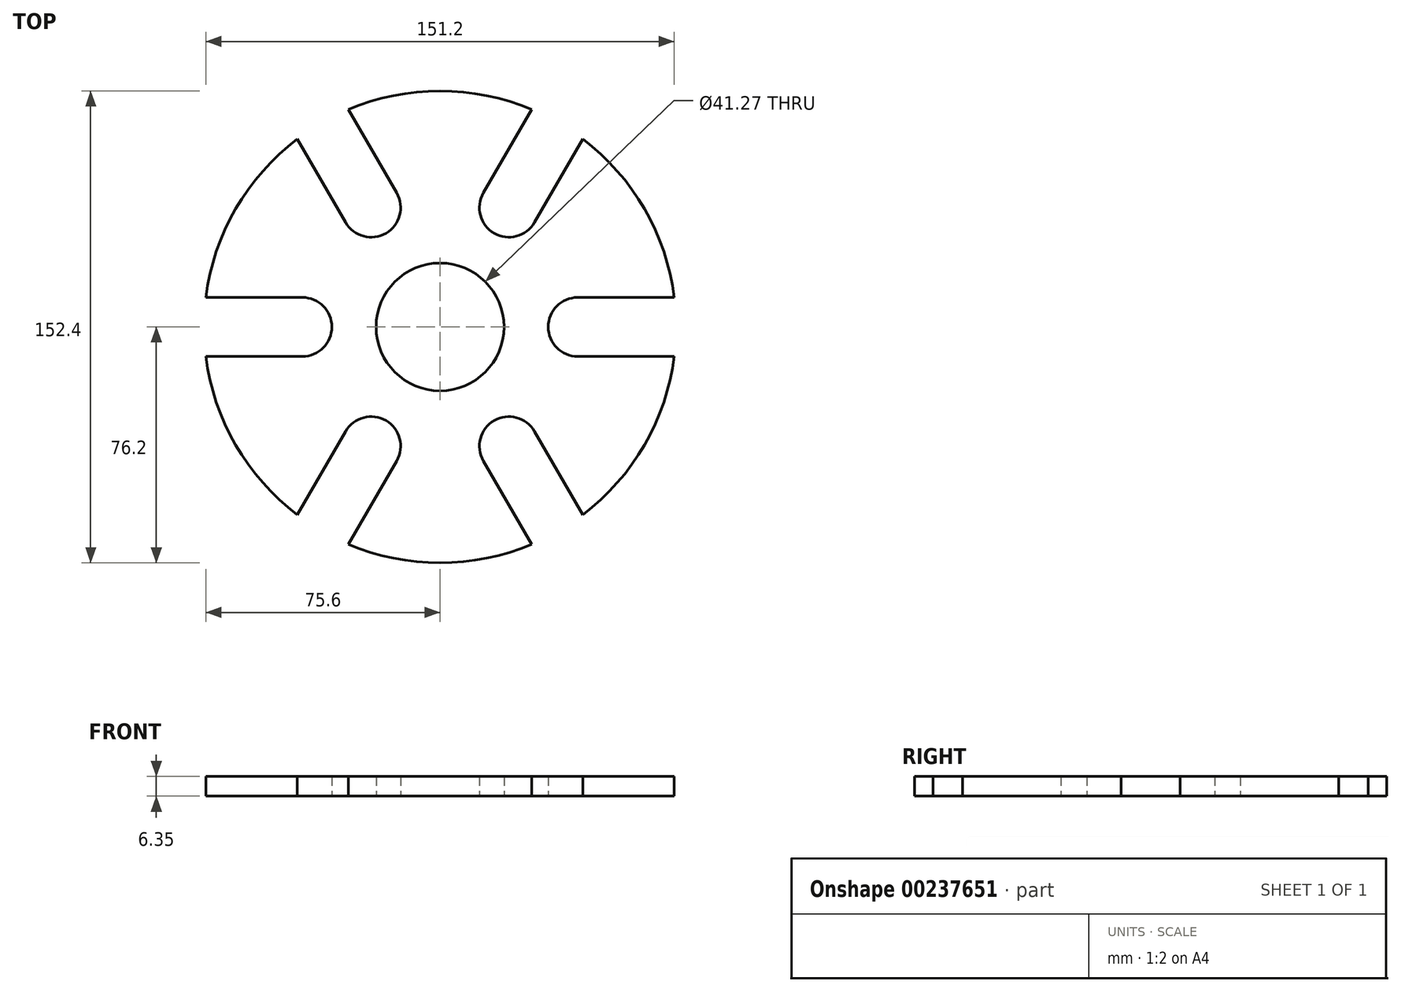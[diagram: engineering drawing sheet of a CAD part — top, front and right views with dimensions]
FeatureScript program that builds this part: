
annotation { "Feature Type Name" : "Feature", "Feature Type Description" : "" }
export const myFeature = defineFeature(function(context is Context, id is Id, definition is map)
    precondition{}
    {
        {
            var Q0;
            Q0=qCreatedBy(makeId("Top.planeOp"),FACE);
            var sketch = newSketch(context, id + "F0", { "sketchPlane" : qUnion([Q0])});
            skArc(sketch, "E0", {"start": v(-75.6, -9.52) * mm, "mid": v(-66, -38.1) * mm, "end": v(-46.05, -60.71) * mm});
            skCircle(sketch, "E1", {"center": v(0, 0) * mm, "radius": 20.64 * mm});
            skArc(sketch, "E2", {"start": v(-44.45, -9.53) * mm, "mid": v(-34.93, 0) * mm, "end": v(-44.45, 9.53) * mm});
            skLineSegment(sketch, "E3", {"start": v(-44.45, 9.53) * mm, "end": v(-75.6, 9.53) * mm});
            skLineSegment(sketch, "E4", {"start": v(-44.45, -9.53) * mm, "end": v(-75.6, -9.53) * mm});
            skLineSegment(sketch, "E5", {"start": v(-75.6, -9.53) * mm, "end": v(-44.45, -9.53) * mm});
            skLineSegment(sketch, "E6.MirrorCS", {"start": v(44.45, -9.53) * mm, "end": v(75.6, -9.53) * mm});
            skArc(sketch, "E7.MirrorC", {"start": v(-75.6, 9.53) * mm, "mid": v(-66, 38.1) * mm, "end": v(-46.05, 60.71) * mm});
            skArc(sketch, "E8.MirrorC", {"start": v(44.45, -9.53) * mm, "mid": v(34.93, 0) * mm, "end": v(44.45, 9.53) * mm});
            skLineSegment(sketch, "E9.MirrorCS", {"start": v(75.6, -9.53) * mm, "end": v(44.45, -9.53) * mm});
            skLineSegment(sketch, "E10.MirrorCS", {"start": v(44.45, 9.53) * mm, "end": v(75.6, 9.53) * mm});
            skArc(sketch, "E11.trimOffspring", {"start": v(75.6, -9.52) * mm, "mid": v(66, -38.1) * mm, "end": v(46.05, -60.71) * mm});
            skArc(sketch, "E12.trimOffspring", {"start": v(75.6, 9.53) * mm, "mid": v(66, 38.1) * mm, "end": v(46.05, 60.71) * mm});
            skArc(sketch, "E13", {"start": v(13.98, 43.26) * mm, "mid": v(17.46, 30.25) * mm, "end": v(30.47, 33.73) * mm});
            skLineSegment(sketch, "E14", {"start": v(30.47, 33.73) * mm, "end": v(46.05, 60.71) * mm});
            skLineSegment(sketch, "E15", {"start": v(46.05, 60.71) * mm, "end": v(30.47, 33.73) * mm});
            skLineSegment(sketch, "E16", {"start": v(13.98, 43.26) * mm, "end": v(29.55, 70.24) * mm});
            skArc(sketch, "E17.trimOffspring", {"start": v(29.55, 70.24) * mm, "mid": v(0, 76.2) * mm, "end": v(-29.55, 70.24) * mm});
            skArc(sketch, "E18.trimOffspring", {"start": v(46.05, 60.71) * mm, "mid": v(66, 38.1) * mm, "end": v(75.6, 9.53) * mm});
            skLineSegment(sketch, "E19.MirrorCS", {"start": v(-13.98, -43.26) * mm, "end": v(-29.55, -70.24) * mm});
            skLineSegment(sketch, "E20.MirrorCS", {"start": v(-30.47, -33.73) * mm, "end": v(-46.05, -60.71) * mm});
            skLineSegment(sketch, "E21.MirrorCS", {"start": v(-29.55, -70.24) * mm, "end": v(-13.98, -43.26) * mm});
            skArc(sketch, "E22.MirrorCS", {"start": v(-30.47, -33.73) * mm, "mid": v(-17.46, -30.25) * mm, "end": v(-13.98, -43.26) * mm});
            skArc(sketch, "E23.trimOffspring", {"start": v(-29.55, -70.24) * mm, "mid": v(0, -76.2) * mm, "end": v(29.55, -70.24) * mm});
            skArc(sketch, "E24.trimOffspring", {"start": v(-46.05, -60.71) * mm, "mid": v(-66, -38.1) * mm, "end": v(-75.6, -9.53) * mm});
            skArc(sketch, "E25", {"start": v(30.47, -33.73) * mm, "mid": v(17.46, -30.25) * mm, "end": v(13.98, -43.26) * mm});
            skLineSegment(sketch, "E26", {"start": v(13.98, -43.26) * mm, "end": v(29.55, -70.24) * mm});
            skLineSegment(sketch, "E27", {"start": v(29.55, -70.24) * mm, "end": v(13.98, -43.26) * mm});
            skLineSegment(sketch, "E28", {"start": v(30.47, -33.73) * mm, "end": v(46.05, -60.71) * mm});
            skArc(sketch, "E29.trimOffspring", {"start": v(29.55, -70.24) * mm, "mid": v(0, -76.2) * mm, "end": v(-29.55, -70.24) * mm});
            skArc(sketch, "E30.trimOffspring", {"start": v(46.05, -60.71) * mm, "mid": v(66, -38.1) * mm, "end": v(75.6, -9.53) * mm});
            skLineSegment(sketch, "E31.MirrorCS", {"start": v(-30.47, 33.73) * mm, "end": v(-46.05, 60.71) * mm});
            skArc(sketch, "E32.MirrorCS", {"start": v(-13.98, 43.26) * mm, "mid": v(-17.46, 30.25) * mm, "end": v(-30.47, 33.73) * mm});
            skLineSegment(sketch, "E33.MirrorCS", {"start": v(-46.05, 60.71) * mm, "end": v(-30.47, 33.73) * mm});
            skLineSegment(sketch, "E34.MirrorCS", {"start": v(-13.98, 43.26) * mm, "end": v(-29.55, 70.24) * mm});
            skPoint(sketch, "E35.orphan", {"position": v(-26.99, -30.25) * mm});
            skPoint(sketch, "E36.2.end.orphan", {"position": v(-39.69, -8.25) * mm});
            skArc(sketch, "E37.trimOffspring", {"start": v(-29.55, 70.24) * mm, "mid": v(0, 76.2) * mm, "end": v(29.55, 70.24) * mm});
            skArc(sketch, "E38.trimOffspring", {"start": v(-46.05, 60.71) * mm, "mid": v(-66, 38.1) * mm, "end": v(-75.6, 9.53) * mm});
            skSolve(sketch);
        }
        {
            var Q0;
            {var subQ2=sQuery(id+"F0.wireOp",EDGE,"E36.4");Q0=makeQuery(id+"F0.imprint","IMPRINT",FACE,{"disambiguationData":[TD([[makeQuery(id+"F0.imprint","IMPRINT",EDGE,{"derivedFrom":subQ2}),1.0]])]});}
            var Q1;
            Q1=makeQuery(id+"F0.imprint","IMPRINT",FACE,{"disambiguationData":[TD([[makeQuery(id+"F0.imprint","IMPRINT",EDGE,{"derivedFrom":sQuery(id+"F0.wireOp",EDGE,"E1")}),-1.0]])]});
            extrude(context, id + "F1", {"entities" : qUnion([Q0, Q1]), "depth" : 6.35 * mm});
        }
    });
